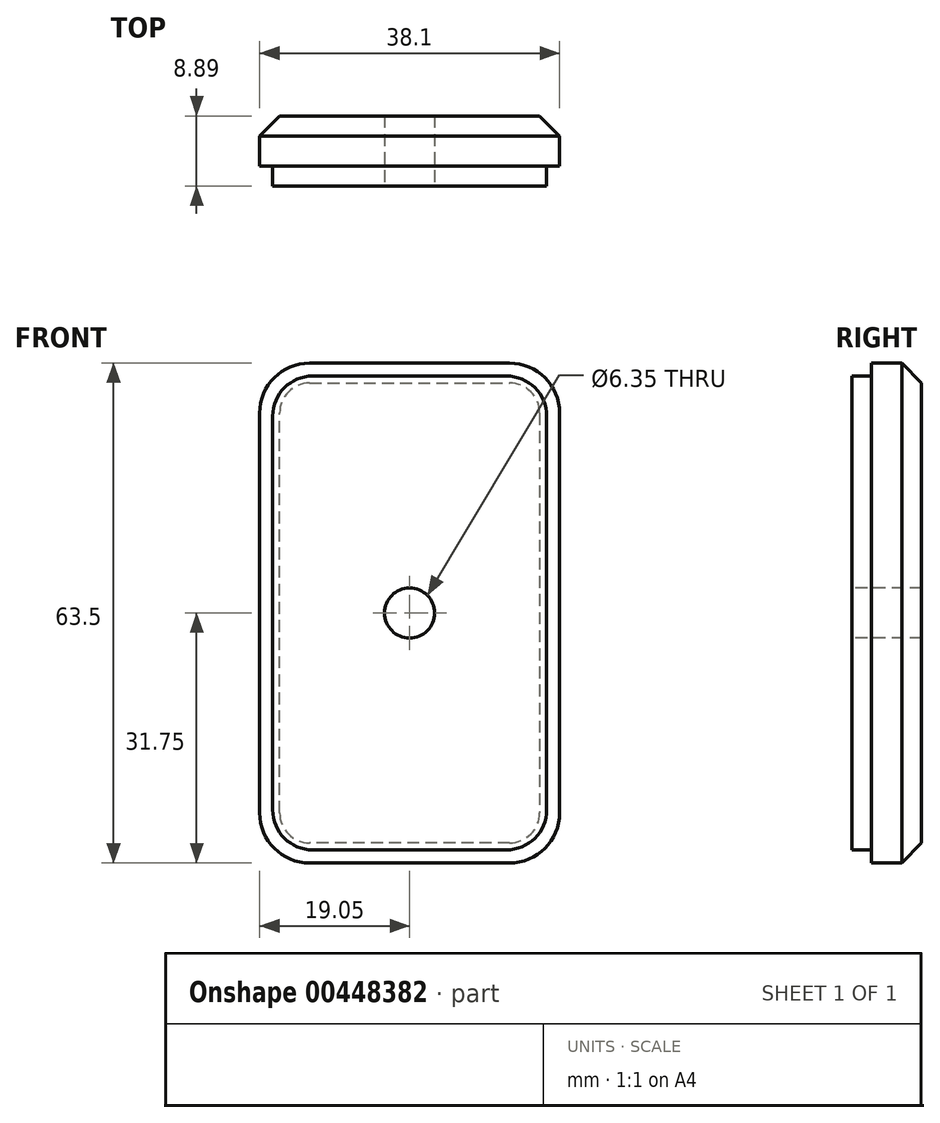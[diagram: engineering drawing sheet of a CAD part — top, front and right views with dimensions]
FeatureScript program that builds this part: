
annotation { "Feature Type Name" : "Feature", "Feature Type Description" : "" }
export const myFeature = defineFeature(function(context is Context, id is Id, definition is map)
    precondition{}
    {
        {
            var Q0;
            Q0=qCreatedBy(makeId("Front.planeOp"),FACE);
            var sketch = newSketch(context, id + "F0", { "sketchPlane" : qUnion([Q0])});
            skLineSegment(sketch, "E0.bottom", {"start": v(12.7, 31.75) * mm, "end": v(-12.7, 31.75) * mm});
            skLineSegment(sketch, "E0.top", {"start": v(12.7, -31.75) * mm, "end": v(-12.7, -31.75) * mm});
            skLineSegment(sketch, "E0.left", {"start": v(19.05, 25.4) * mm, "end": v(19.05, -25.4) * mm});
            skLineSegment(sketch, "E0.right", {"start": v(-19.05, 25.4) * mm, "end": v(-19.05, -25.4) * mm});
            skPoint(sketch, "E0.middle", {"position": v(0, 0) * mm});
            skPoint(sketch, "E1.visualSharp", {"position": v(-19.05, 31.75) * mm});
            skArc(sketch, "E1.filletArc", {"start": v(-12.7, 31.75) * mm, "mid": v(-17.2, 29.9) * mm, "end": v(-19.05, 25.4) * mm});
            skPoint(sketch, "E2.visualSharp", {"position": v(19.05, 31.75) * mm});
            skArc(sketch, "E2.filletArc", {"start": v(19.05, 25.4) * mm, "mid": v(17.2, 29.9) * mm, "end": v(12.7, 31.75) * mm});
            skPoint(sketch, "E3.visualSharp", {"position": v(19.05, -31.75) * mm});
            skArc(sketch, "E3.filletArc", {"start": v(12.7, -31.75) * mm, "mid": v(17.2, -29.9) * mm, "end": v(19.05, -25.4) * mm});
            skPoint(sketch, "E4.visualSharp", {"position": v(-19.05, -31.75) * mm});
            skArc(sketch, "E4.filletArc", {"start": v(-19.05, -25.4) * mm, "mid": v(-17.2, -29.9) * mm, "end": v(-12.7, -31.75) * mm});
            skSolve(sketch);
        }
        {
            var Q0;
            Q0 = qSketchRegion(id + "F0", true);
            extrude(context, id + "F1", {"entities" : qUnion([Q0]), "depth" : 6.35 * mm});
        }
        {
            var Q0;
            Q0=makeQuery(id+"F1.opExtrude","CAP_FACE",FACE,{"disambiguationData":[OSD([sQuery(id+"F0.wireOp",EDGE,"E0.bottom"),sQuery(id+"F0.wireOp",EDGE,"E0.top"),sQuery(id+"F0.wireOp",EDGE,"E0.left"),sQuery(id+"F0.wireOp",EDGE,"E0.right"),sQuery(id+"F0.wireOp",EDGE,"E1.filletArc"),sQuery(id+"F0.wireOp",EDGE,"E2.filletArc"),sQuery(id+"F0.wireOp",EDGE,"E3.filletArc"),sQuery(id+"F0.wireOp",EDGE,"E4.filletArc")])],"isStart":false});
            var sketch = newSketch(context, id + "F2", { "sketchPlane" : qUnion([Q0])});
            skCircle(sketch, "E5", {"center": v(0, 0) * mm, "radius": 3.18 * mm});
            skSolve(sketch);
        }
        {
            var Q0;
            Q0 = qSketchRegion(id + "F2", true);
            extrude(context, id + "F3", {"entities" : qUnion([Q0]), "operationType" : NewBodyOperationType.REMOVE, "oppositeDirection" : true, "depth" : 25.4 * mm});
        }
        {
            var Q0;
            Q0=makeQuery(id+"F1.opExtrude","CAP_FACE",FACE,{"disambiguationData":[OSD([sQuery(id+"F0.wireOp",EDGE,"E0.bottom"),sQuery(id+"F0.wireOp",EDGE,"E0.top"),sQuery(id+"F0.wireOp",EDGE,"E0.left"),sQuery(id+"F0.wireOp",EDGE,"E0.right"),sQuery(id+"F0.wireOp",EDGE,"E1.filletArc"),sQuery(id+"F0.wireOp",EDGE,"E2.filletArc"),sQuery(id+"F0.wireOp",EDGE,"E3.filletArc"),sQuery(id+"F0.wireOp",EDGE,"E4.filletArc")])],"isStart":false});
            var sketch = newSketch(context, id + "F4", { "sketchPlane" : qUnion([Q0])});
            skLineSegment(sketch, "E6.0", {"start": v(-17.4, 25.02) * mm, "end": v(-17.4, -25.02) * mm});
            skLineSegment(sketch, "E6.1", {"start": v(12.32, 30.1) * mm, "end": v(-12.32, 30.1) * mm});
            skLineSegment(sketch, "E6.2", {"start": v(17.4, 25.02) * mm, "end": v(17.4, -25.02) * mm});
            skLineSegment(sketch, "E6.3", {"start": v(12.32, -30.1) * mm, "end": v(-12.32, -30.1) * mm});
            skPoint(sketch, "E7.visualSharp", {"position": v(-17.4, 30.1) * mm});
            skArc(sketch, "E7.filletArc", {"start": v(-12.32, 30.1) * mm, "mid": v(-15.91, 28.61) * mm, "end": v(-17.4, 25.02) * mm});
            skPoint(sketch, "E8.visualSharp", {"position": v(17.4, 30.1) * mm});
            skArc(sketch, "E8.filletArc", {"start": v(17.4, 25.02) * mm, "mid": v(15.91, 28.61) * mm, "end": v(12.32, 30.1) * mm});
            skPoint(sketch, "E9.visualSharp", {"position": v(17.4, -30.1) * mm});
            skArc(sketch, "E9.filletArc", {"start": v(12.32, -30.1) * mm, "mid": v(15.91, -28.61) * mm, "end": v(17.4, -25.02) * mm});
            skPoint(sketch, "E10.visualSharp", {"position": v(-17.4, -30.1) * mm});
            skArc(sketch, "E10.filletArc", {"start": v(-17.4, -25.02) * mm, "mid": v(-15.91, -28.61) * mm, "end": v(-12.32, -30.1) * mm});
            skSolve(sketch);
        }
        {
            var Q0;
            Q0=makeQuery(id+"F4.imprint","IMPRINT",FACE,{"disambiguationData":[TD([[makeQuery(id+"F4.imprint","IMPRINT",EDGE,{"derivedFrom":sQuery(id+"F4.wireOp",EDGE,"E6.0")}),1.0]])]});
            extrude(context, id + "F5", {"entities" : qUnion([Q0]), "operationType" : NewBodyOperationType.ADD, "depth" : 2.54 * mm});
        }
        {
            var Q0;
            Q0=makeQuery(id+"F1.opExtrude","CAP_EDGE",EDGE,{"disambiguationData":[OSD([sQuery(id+"F0.wireOp",EDGE,"E0.right")])],"isStart":true});
            chamfer(context, id + "F6", {"entities" : qUnion([Q0]), "width" : 2.54 * mm, "tangentPropagation" : true});
        }
    });
